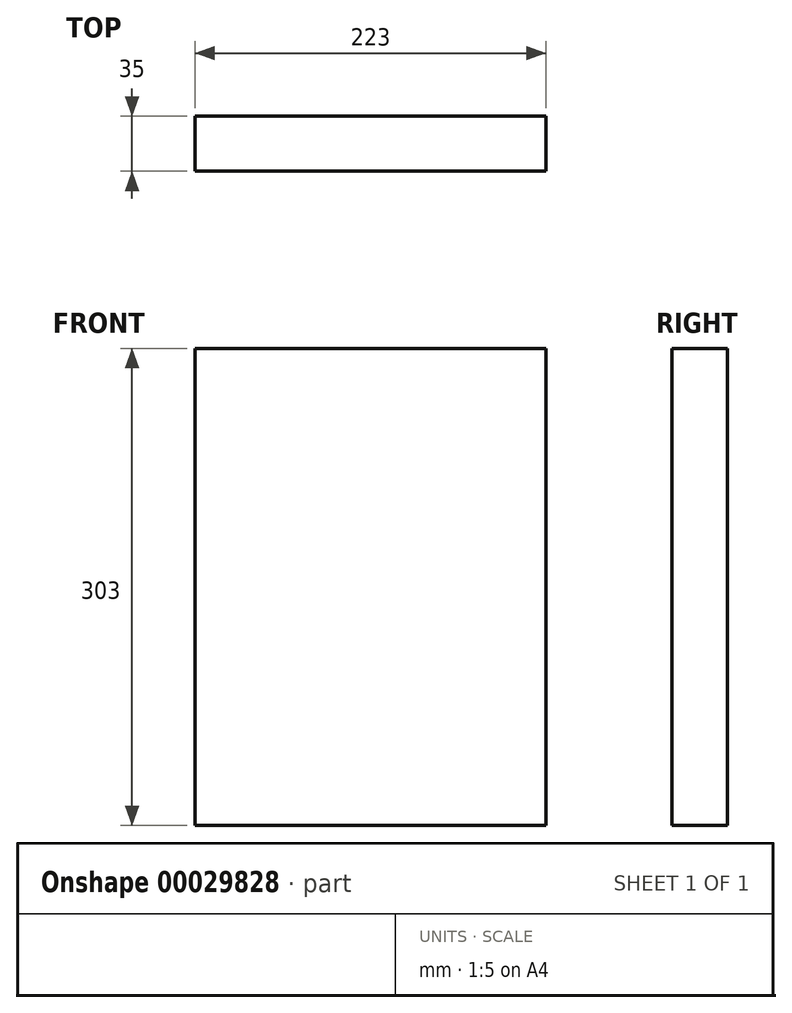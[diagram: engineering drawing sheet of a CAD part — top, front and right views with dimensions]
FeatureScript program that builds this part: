
annotation { "Feature Type Name" : "Feature", "Feature Type Description" : "" }
export const myFeature = defineFeature(function(context is Context, id is Id, definition is map)
    precondition{}
    {
        {
            var Q0;
            Q0=qCreatedBy(makeId("Front.planeOp"),FACE);
            var sketch = newSketch(context, id + "F0", { "sketchPlane" : qUnion([Q0])});
            skLineSegment(sketch, "E0.rect.bottom", {"start": v(-111.5, 151.5) * mm, "end": v(111.5, 151.5) * mm});
            skLineSegment(sketch, "E0.rect.top", {"start": v(-111.5, -151.5) * mm, "end": v(111.5, -151.5) * mm});
            skLineSegment(sketch, "E0.rect.left", {"start": v(-111.5, 151.5) * mm, "end": v(-111.5, -151.5) * mm});
            skLineSegment(sketch, "E0.rect.right", {"start": v(111.5, 151.5) * mm, "end": v(111.5, -151.5) * mm});
            skPoint(sketch, "E0.rect.middle", {"position": v(0, 0) * mm});
            skSolve(sketch);
        }
        {
            var Q0;
            Q0=qSketchRegion(id+"F0",true);
            extrude(context, id + "F1", {"entities" : qUnion([Q0]), "endBound" : BoundingType.SYMMETRIC, "depth" : 35 * mm});
        }
    });
